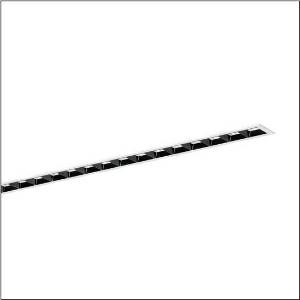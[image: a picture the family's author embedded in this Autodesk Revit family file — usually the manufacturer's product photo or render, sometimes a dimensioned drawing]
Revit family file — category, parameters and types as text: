
# Revit family: silica_r__21_51mx14tbt5w_b174
name_source: partatom
category: Lighting Fixtures
units: mm (PartAtom-declared; Revit-internal decimal feet)

## family parameters
Cut with Voids When Loaded = No
Host = Face
Light Source = No
Part Type = Normal
Room Calculation Point = No
Round Connector Dimension = Use Diameter
Shared = No

## types (1)
- --- (1 x LED, 4100 lm, 40.5 W, 6500K)
    Apparent Load = 41 VA
    CIE Flux Codes = 74 94 99 100 100
    Color Rendering = 80
    Color Temperature = 6500K
    Default Elevation = 1800 mm
    Description = Silica® 21, office luminaire, primary light control with darklight reflector, of PMMA, black, light emission: direct distribution, primary light characteristic: asymmetric, installation type: recessed, LED, rated luminous flux: 4.100lm, luminous efficacy: 96lm/W, light colour: 8tw, colour temperature: 2700..6500K, control gear: DALI DT8, with terminal, 3+2-pole, max. 2.5mm², mains connection: 220..240V, AC, 50/60Hz, rated input power: 42.6W, luminaire housing, of aluminium, traffic white (RAL 9016), length: 1.528mm, width: 79mm, height: 53mm, protection rating (complete): IP20, insulation class (complete): insulation class I (protective earthing), certification: CE, ENEC, VDE, permissible operating ambient temperature: 0..+35°C, standard: EN 50419, packaging unit: 1 piece
    Height = 0 mm  [stored 0 ft]
    Lamp = 1 x LED
    Lamp Light Flux = 4100 lm
    Lamp Power = 40.5 W
    Lamp count = 1
    Length = 1527 mm
    Luminous efficacy = 101 lm/W
    Manufacturer = Siteco
    ModVariant = No
    Model = 51MX14TBT5W
    Mounting Place = Ceiling
    Mounting Type = Recessed
    Number of Poles = 1
    OnlyDefault = Yes
    Power Factor = 1
    Product Name = Silica® 21
    Product group = office luminaire | ceiling recessed
    ProductGroupID = 401
    Protection Class = Protection class I
    Protection Degree = IP 20
    RLX_Detail_Level = 1
    RLX_Emergency_Light_Flux = 0 lm
    RLX_Emergency_Type = 0
    RLX_Emergency_Type_DB = No
    RlxData = <blob elided: 39389 chars, md5=ee540681>
    Socket = socket
    Standby Power = 0 W
    System Light Flux = 4100 lm
    System Power = 41 W
    Type Comments = individual setting
    Type Image = l_1335880.jpg
    URL = http://relux.com
    VarID = @adj_140028
    Voltage = 0 V
    Weight = 0.00 kg
    Width = 79 mm

note: [stored X ft] marks values corroborated as IEEE doubles in the binary element streams (Revit-internal decimal feet)

## geometry (parser evidence)
native form markers: Blend x4, Sweep x10
no freeform markers — native parametric forms only
